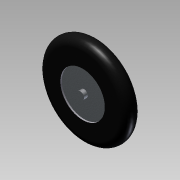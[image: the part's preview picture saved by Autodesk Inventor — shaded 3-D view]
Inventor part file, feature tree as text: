
AUTODESK INVENTOR PART (.ipt)
format: ipt  version: 2013 (Build 170138000, 138)  size: 140,288 bytes
history: native  units: in
note: dims shown in document units (in); Inventor stores cm internally (conversion verified against a paired STEP export)
features: extrude x5, sketch x5, fillet x1
ambient origin geometry x8: Origin, YZ Plane, XZ Plane, XY Plane, X Axis, Y Axis, Z Axis, Center Point
bodies: Solid1 (feature_tree)
feature tree (11):
  extrude  "Extrusion1"  Depth=1.0in TaperAngle=0.0deg
  extrude  "Extrusion2"  Depth=0.1in TaperAngle=0.0deg
  extrude  "Extrusion3"  Depth=0.1in TaperAngle=0.0deg
  fillet  "Fillet1"  Radius=0.5in
  extrude  "Extrusion4"  Depth=0.25in TaperAngle=0.0deg
  extrude  "Extrusion5"  Depth=0.25in TaperAngle=0.0deg
  sketch  "Sketch1"  dims[d0=6.0in d1=1.0in d2=0.0in]
  sketch  "Sketch2"  dims[d3=3.0in d4=0.1in d5=0.0in]
  sketch  "Sketch3"  dims[d6=3.0in d7=0.1in d8=0.0in d9=0.5in]
  sketch  "Sketch4"  dims[d10=0.5in d11=0.25in d12=0.0in]
  sketch  "Sketch5"  dims[d13=0.5in d14=0.25in d15=0.0in]
